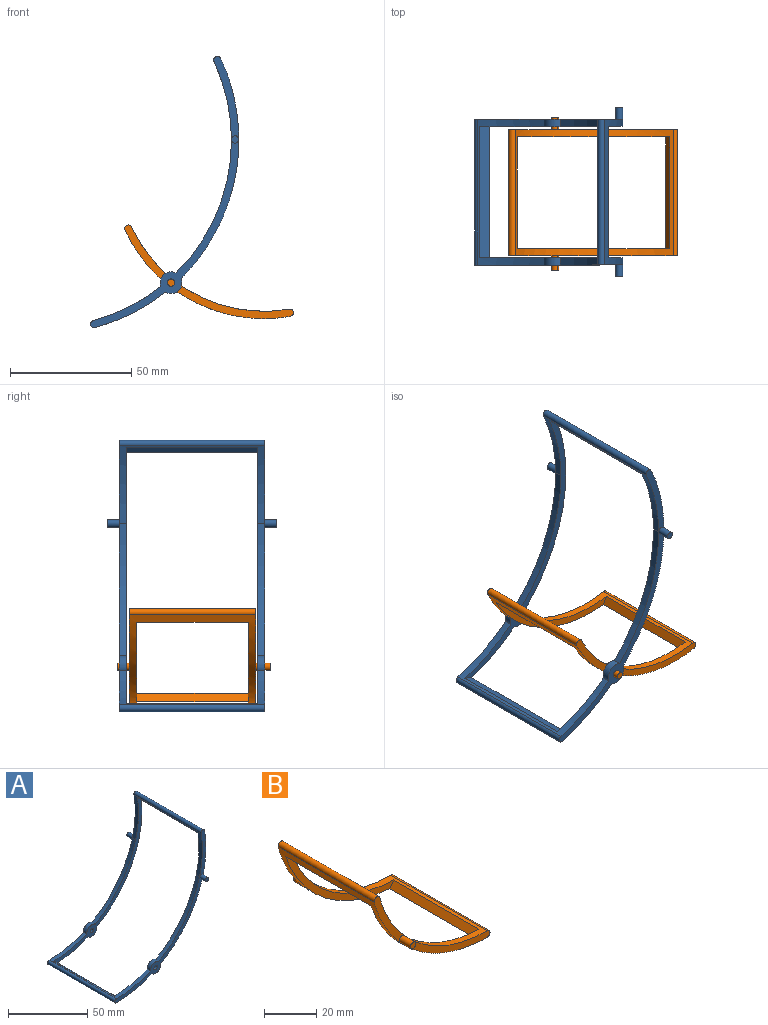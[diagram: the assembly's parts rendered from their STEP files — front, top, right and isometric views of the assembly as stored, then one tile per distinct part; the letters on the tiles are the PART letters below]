
ASSEMBLY  parts=2 mates=1
PART A: 24 faces, bbox 81.3x70x94.9 mm
  f0: cylinder r=76.82mm len=47.19mm, axis (0,1,0), area 183.3mm2, adj f1,f4,f16,f23
  f1: cylinder r=4.5mm len=7.54mm, axis (0,1,0), area 32.5mm2, adj f0,f8,f16,f23
  f2: cylinder r=4.5mm len=7.71mm, axis (0,1,0), area 34mm2, adj f10,f12,f16,f23
  f3: cylinder r=1.55mm len=3.1mm, axis (0,1,0), area 29.2mm2, adj f16,f23
  f4: cylinder r=1.5mm len=8mm, axis (0,-1,0), area 47.2mm2, adj f0,f6,f16,f18,f23
  f5: cylinder r=76.82mm len=47.19mm, axis (0,1,0), area 183.3mm2, adj f7,f15,f17,f22
  f6: cylinder r=76.82mm len=60mm, axis (0,1,0), area 257.4mm2, adj f4,f13,f15,f16,f17,f21,f22,f23
  f7: cylinder r=4.5mm len=7.54mm, axis (0,1,0), area 32.5mm2, adj f5,f8,f15,f22
  f8: cylinder r=76.82mm len=60mm, axis (0,1,0), area 246.8mm2, adj f1,f7,f9,f15,f16,f20,f22,f23
  f9: cylinder r=1.5mm len=60mm, axis (0,1,0), area 282.7mm2, adj f8,f10,f15,f16
  f10: cylinder r=79.82mm len=60mm, axis (0,1,0), area 440.1mm2, adj f2,f9,f11,f15,f16,f20,f22,f23
  f11: cylinder r=4.5mm len=7.71mm, axis (0,1,0), area 34mm2, adj f10,f12,f15,f22
  f12: cylinder r=79.82mm len=83.26mm, axis (0,1,0), area 832.3mm2, adj f2,f11,f13,f15,f16,f21,f22,f23
  f13: cylinder r=1.5mm len=60mm, axis (0,1,0), area 282.7mm2, adj f6,f12,f15,f16
  f14: cylinder r=1.55mm len=3.1mm, axis (0,1,0), area 29.2mm2, adj f15,f22
  f15: plane 94.93x81.32mm, normal (0,-1,0), area 439.7mm2, adj f5,f6,f7,f8,f9,f10,f11,f12
  f16: plane 94.93x81.32mm, normal (0,1,0), area 439.7mm2, adj f0,f1,f2,f3,f4,f6,f8,f9
  f17: cylinder r=1.5mm len=8mm, axis (0,-1,0), area 47.2mm2, adj f5,f6,f15,f19,f22
  f18: plane 3x3mm, normal (0,1,0), area 7.1mm2, adj f4
  f19: plane 3x3mm, normal (0,-1,0), area 7.1mm2, adj f17
  f20: plane 54x3.43mm, normal (0.64,0,0.77), area 241.9mm2, adj f8,f10,f22,f23
  f21: plane 54x3.43mm, normal (-0.64,0,-0.77), area 241.9mm2, adj f6,f12,f22,f23
  f22: plane 91.97x78.74mm, normal (0,1,0), area 422.8mm2, adj f5,f6,f7,f8,f10,f11,f12,f14
  f23: plane 91.97x78.74mm, normal (0,-1,0), area 422.8mm2, adj f0,f1,f2,f3,f4,f6,f8,f10
PART B: 14 faces, bbox 62.5x63x48.7 mm
  f0: cylinder r=60.1mm len=63mm, axis (0,1,0), area 607.3mm2, adj f2,f3,f4,f5,f6,f7,f8,f9
  f1: cylinder r=63.1mm len=60.95mm, axis (0,1,0), area 836mm2, adj f2,f3,f4,f5,f10,f11,f12,f13
  f2: cylinder r=1.5mm len=52mm, axis (0,1,0), area 245mm2, adj f0,f1,f4,f5
  f3: cylinder r=1.5mm len=52mm, axis (0,1,0), area 245mm2, adj f0,f1,f4,f5
  f4: plane 62.5x48.66mm, normal (0,-1,0), area 241.9mm2, adj f0,f1,f2,f3,f8
  f5: plane 62.5x48.66mm, normal (0,1,0), area 241.9mm2, adj f0,f1,f2,f3,f7
  f6: plane 3x3mm, normal (0,1,0), area 7.1mm2, adj f0,f7
  f7: cylinder r=1.5mm len=5mm, axis (0,-1,0), area 46.9mm2, adj f0,f5,f6
  f8: cylinder r=1.5mm len=6mm, axis (0,-1,0), area 56.3mm2, adj f0,f4,f9
  f9: plane 3x3mm, normal (0,-1,0), area 7.1mm2, adj f0,f8
  f10: plane 58.42x46.03mm, normal (0,1,0), area 226.4mm2, adj f0,f1,f11,f13
  f11: plane 46x2.91mm, normal (0.79,0,-0.61), area 168.7mm2, adj f0,f1,f10,f12
  f12: plane 58.42x46.03mm, normal (0,-1,0), area 226.4mm2, adj f0,f1,f11,f13
  f13: plane 46x2.91mm, normal (-0.79,0,0.61), area 168.7mm2, adj f0,f1,f10,f12
PLACE A rot(axis=(0,-1,0),15deg) t=(-181.09,-16.16,27.74)mm
PLACE B rot(axis=(0,-1,0),10deg) t=(56.79,-20.36,43.48)mm
MATE cylindrical B.f7 <-> A.f1  axis (0,-1,0) through (-129.15,-78.36,-30.88)mm
